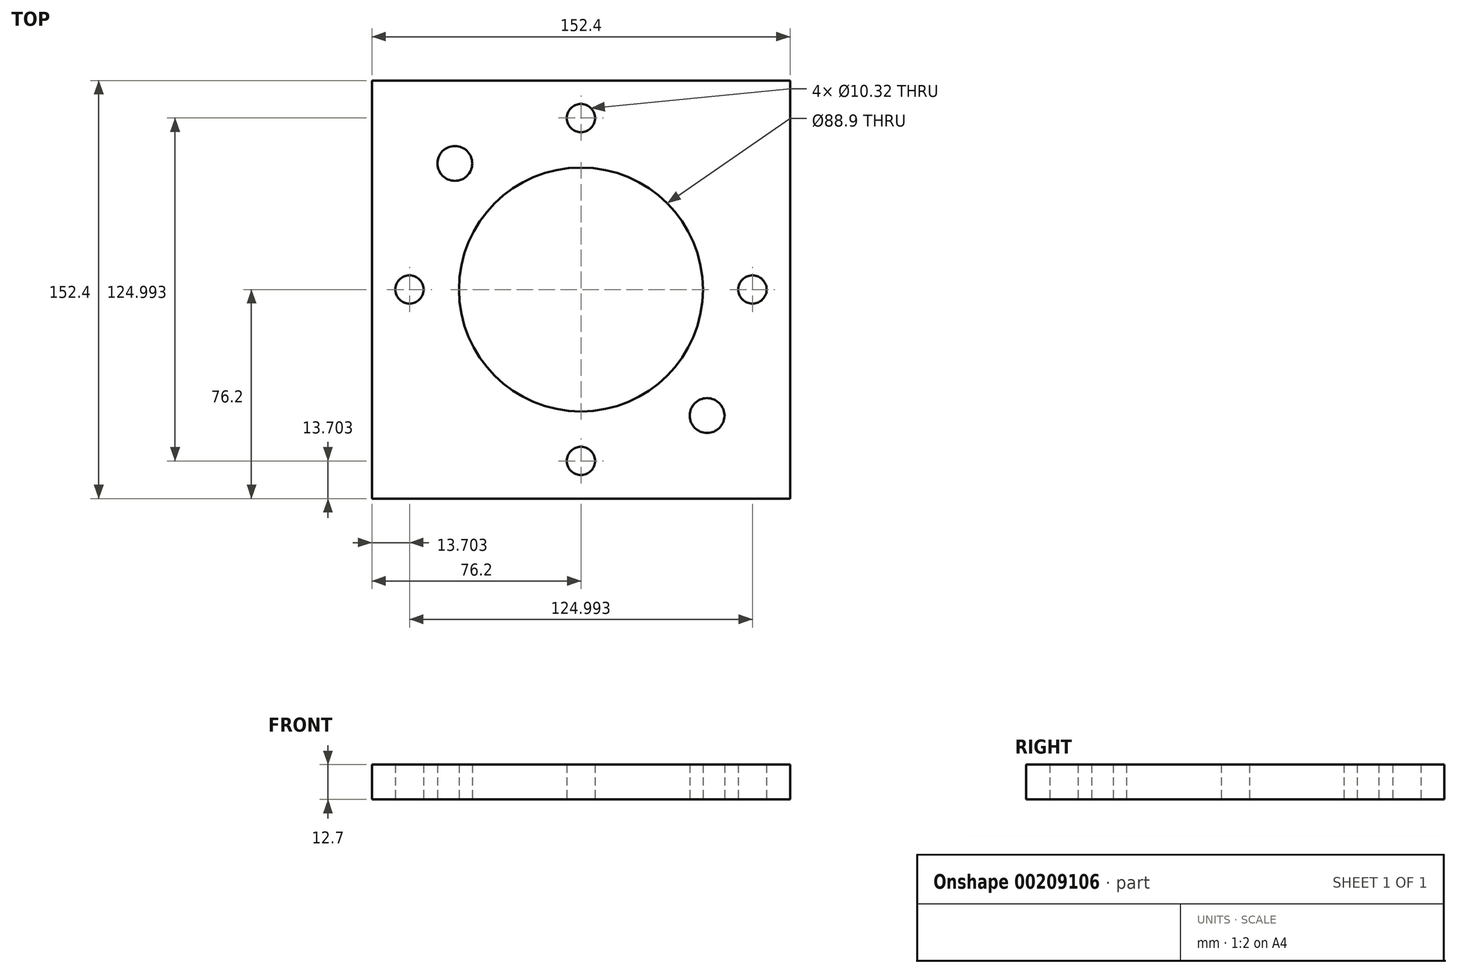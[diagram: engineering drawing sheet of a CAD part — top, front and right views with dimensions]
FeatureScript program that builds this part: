
annotation { "Feature Type Name" : "Feature", "Feature Type Description" : "" }
export const myFeature = defineFeature(function(context is Context, id is Id, definition is map)
    precondition{}
    {
        {
            var Q0;
            Q0=qCreatedBy(makeId("Top.planeOp"),FACE);
            var sketch = newSketch(context, id + "F0", { "sketchPlane" : qUnion([Q0])});
            skLineSegment(sketch, "E0.bottom", {"start": v(76.2, 76.2) * mm, "end": v(-76.2, 76.2) * mm});
            skLineSegment(sketch, "E0.top", {"start": v(76.2, -76.2) * mm, "end": v(-76.2, -76.2) * mm});
            skLineSegment(sketch, "E0.left", {"start": v(76.2, 76.2) * mm, "end": v(76.2, -76.2) * mm});
            skLineSegment(sketch, "E0.right", {"start": v(-76.2, 76.2) * mm, "end": v(-76.2, -76.2) * mm});
            skPoint(sketch, "E0.middle", {"position": v(0, 0) * mm});
            skCircle(sketch, "E1", {"center": v(0, 0) * mm, "radius": 62.5 * mm, "construction": true});
            skLineSegment(sketch, "E2", {"start": v(0, 73.2) * mm, "end": v(0, -70.98) * mm, "construction": true});
            skLineSegment(sketch, "E3.anchor1", {"start": v(0, 0) * mm, "end": v(0, 62.5) * mm, "construction": true});
            skCircle(sketch, "E4", {"center": v(0, 62.5) * mm, "radius": 5.16 * mm});
            skCircle(sketch, "E5.1.0", {"center": v(62.5, 0) * mm, "radius": 5.16 * mm});
            skCircle(sketch, "E5.2.0", {"center": v(0, -62.5) * mm, "radius": 5.16 * mm});
            skCircle(sketch, "E5.3.0", {"center": v(-62.5, 0) * mm, "radius": 5.16 * mm});
            skLineSegment(sketch, "E5.anchor2", {"start": v(0, 0) * mm, "end": v(-62.5, 0) * mm, "construction": true});
            skLineSegment(sketch, "E6", {"start": v(0, 0) * mm, "end": v(-76.2, 76.2) * mm, "construction": true});
            skCircle(sketch, "E7", {"center": v(0, 0) * mm, "radius": 65 * mm, "construction": true});
            skCircle(sketch, "E8", {"center": v(-45.96, 45.96) * mm, "radius": 6.35 * mm});
            skCircle(sketch, "E9.1.0", {"center": v(45.96, -45.96) * mm, "radius": 6.35 * mm});
            skCircle(sketch, "E10", {"center": v(0, 0) * mm, "radius": 44.45 * mm});
            skSolve(sketch);
        }
        {
            var Q0;
            Q0=makeQuery(id+"F0.imprint","IMPRINT",FACE,{"disambiguationData":[TD([[makeQuery(id+"F0.imprint","IMPRINT",EDGE,{"derivedFrom":sQuery(id+"F0.wireOp",EDGE,"E0.bottom")}),1.0]])]});
            extrude(context, id + "F1", {"entities" : qUnion([Q0]), "depth" : 12.7 * mm});
        }
    });
